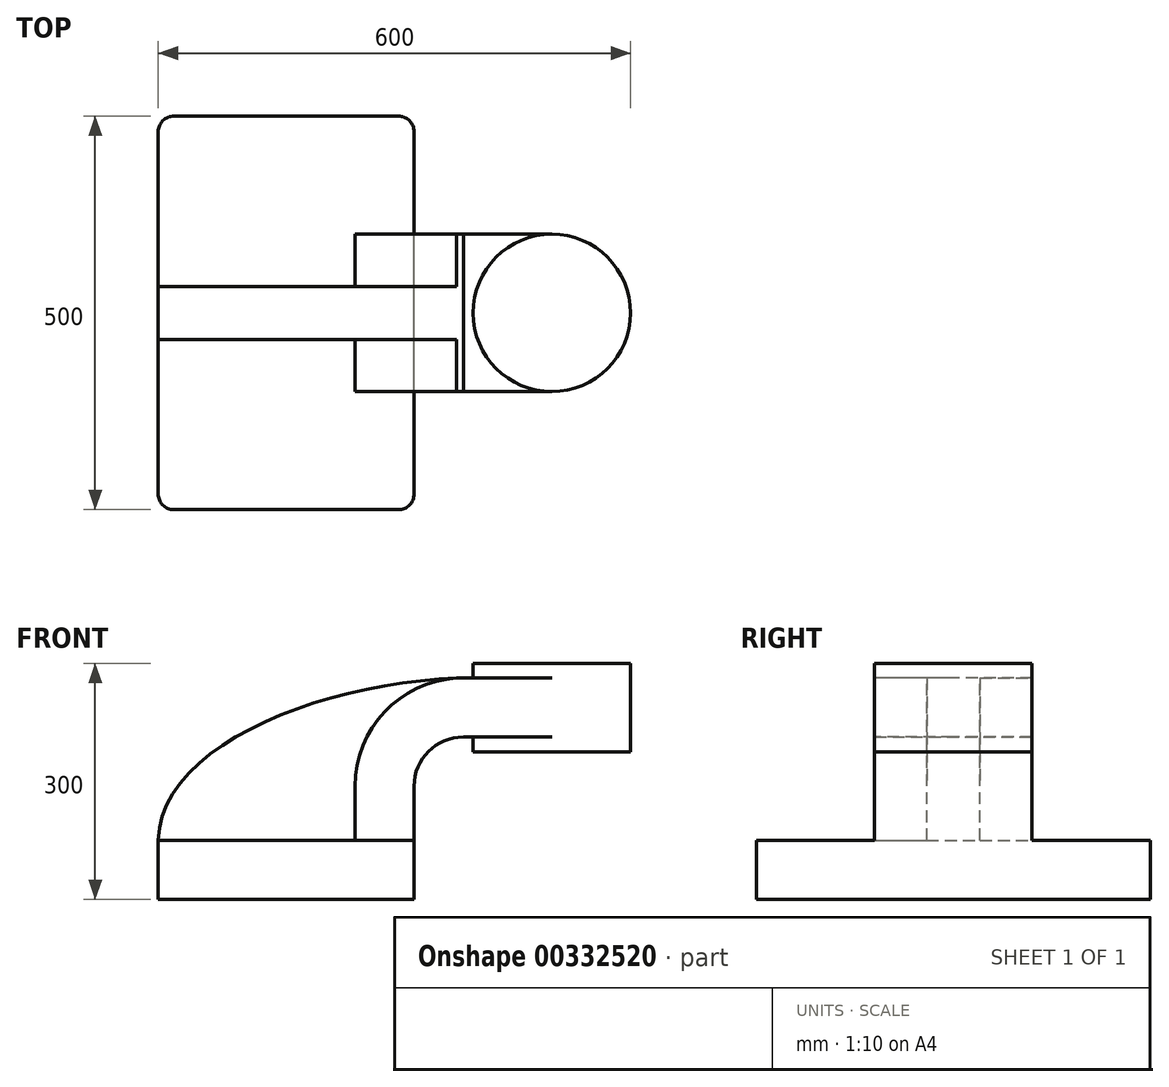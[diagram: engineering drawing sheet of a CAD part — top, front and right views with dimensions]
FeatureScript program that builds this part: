
annotation { "Feature Type Name" : "Feature", "Feature Type Description" : "" }
export const myFeature = defineFeature(function(context is Context, id is Id, definition is map)
    precondition{}
    {
        {
            var Q0;
            Q0=qCreatedBy(makeId("Front.planeOp"),FACE);
            var sketch = newSketch(context, id + "F0", { "sketchPlane" : qUnion([Q0])});
            skLineSegment(sketch, "E0.bottom", {"start": v(-162.5, -37.5) * mm, "end": v(162.5, -37.5) * mm});
            skLineSegment(sketch, "E0.top", {"start": v(-162.5, 37.5) * mm, "end": v(162.5, 37.5) * mm});
            skLineSegment(sketch, "E0.left", {"start": v(-162.5, -37.5) * mm, "end": v(-162.5, 37.5) * mm});
            skLineSegment(sketch, "E0.right", {"start": v(162.5, -37.5) * mm, "end": v(162.5, 37.5) * mm});
            skPoint(sketch, "E0.middle", {"position": v(0, 0) * mm});
            skLineSegment(sketch, "E1.bottom", {"start": v(437.5, 150) * mm, "end": v(237.5, 150) * mm});
            skLineSegment(sketch, "E1.top", {"start": v(437.5, 262.5) * mm, "end": v(237.5, 262.5) * mm});
            skLineSegment(sketch, "E1.left", {"start": v(437.5, 150) * mm, "end": v(437.5, 262.5) * mm});
            skLineSegment(sketch, "E1.right", {"start": v(237.5, 150) * mm, "end": v(237.5, 262.5) * mm});
            skPoint(sketch, "E1.middle", {"position": v(337.5, 206.25) * mm});
            skLineSegment(sketch, "E2", {"start": v(162.5, 37.5) * mm, "end": v(162.5, 106.3) * mm});
            skArc(sketch, "E3", {"start": v(162.5, 106.3) * mm, "mid": v(180.8, 150.5) * mm, "end": v(225, 168.8) * mm});
            skLineSegment(sketch, "E4", {"start": v(225, 168.8) * mm, "end": v(337.5, 168.8) * mm});
            skLineSegment(sketch, "E5.0", {"start": v(225, 243.8) * mm, "end": v(337.5, 243.8) * mm});
            skArc(sketch, "E5.1", {"start": v(87.5, 106.3) * mm, "mid": v(127.77, 203.53) * mm, "end": v(225, 243.8) * mm});
            skLineSegment(sketch, "E5.2", {"start": v(87.5, 37.5) * mm, "end": v(87.5, 106.3) * mm});
            skLineSegment(sketch, "E6", {"start": v(337.5, 150) * mm, "end": v(337.5, 262.5) * mm});
            skFitSpline(sketch, "E7", {"points": [v(-162.5, 37.5) * mm, v(225, 243.8) * mm], "startDerivative": vector(6.8, 368.5) * mm, "endDerivative": vector(520.4, 12.57) * mm});
            skSolve(sketch);
        }
        {
            var Q0;
            Q0=makeQuery(id+"F0.imprint","IMPRINT",FACE,{"disambiguationData":[TD([[makeQuery(id+"F0.imprint","IMPRINT",EDGE,{"derivedFrom":sQuery(id+"F0.wireOp",EDGE,"E0.bottom")}),1.0]])]});
            extrude(context, id + "F1", {"entities" : qUnion([Q0]), "endBound" : BoundingType.SYMMETRIC, "depth" : 500 * mm});
        }
        {
            var Q0;
            {var subQ1=sQuery(id+"F0.wireOp",EDGE,"E2");Q0=makeQuery(id+"F0.imprint","IMPRINT",FACE,{"disambiguationData":[TD([[makeQuery(id+"F0.imprint","IMPRINT",EDGE,{"derivedFrom":subQ1}),1.0]])]});}
            var Q1;
            {var subQ0=sQuery(id+"F0.wireOp",EDGE,"E4");var subQ1=sQuery(id+"F0.wireOp",EDGE,"E1.right");var subQ2=makeQuery(id+"F0.imprint","INTERSECT",VERTEX,{"derivedFrom":[subQ1,subQ0]});Q1=makeQuery(id+"F0.imprint","IMPRINT",FACE,{"disambiguationData":[TD([[makeQuery(id+"F0.imprint","IMPRINT",EDGE,{"disambiguationData":[TD([[subQ2,-1.0]])],"derivedFrom":subQ1}),-1.0]])]});}
            extrude(context, id + "F2", {"entities" : qUnion([Q0, Q1]), "operationType" : NewBodyOperationType.ADD, "endBound" : BoundingType.SYMMETRIC, "depth" : 200 * mm});
        }
        {
            var Q0;
            {var subQ3=sQuery(id+"F0.wireOp",EDGE,"E5.2");Q0=makeQuery(id+"F0.imprint","IMPRINT",FACE,{"disambiguationData":[TD([[makeQuery(id+"F0.imprint","IMPRINT",EDGE,{"derivedFrom":subQ3}),1.0]])]});}
            extrude(context, id + "F3", {"entities" : qUnion([Q0]), "operationType" : NewBodyOperationType.ADD, "endBound" : BoundingType.SYMMETRIC, "depth" : 67.5 * mm});
        }
        {
            var Q0;
            {var subQ0=sQuery(id+"F0.wireOp",EDGE,"E1.left");Q0=makeQuery(id+"F0.imprint","IMPRINT",FACE,{"disambiguationData":[TD([[makeQuery(id+"F0.imprint","IMPRINT",EDGE,{"derivedFrom":subQ0}),1.0]])]});}
            var Q1;
            Q1=sQuery(id+"F0.wireOp",EDGE,"E6");
            revolve(context, id + "F4", {"operationType" : NewBodyOperationType.ADD, "entities" : qUnion([Q0]), "axis" : qUnion([Q1]), "revolveType" : RevolveType.FULL});
        }
        {
            var Q0;
            Q0=makeQuery(id+"F1.opExtrude","CAP_EDGE",EDGE,{"disambiguationData":[OSD([sQuery(id+"F0.wireOp",EDGE,"E0.right")])],"isStart":false});
            var Q1;
            Q1=makeQuery(id+"F1.opExtrude","CAP_EDGE",EDGE,{"disambiguationData":[OSD([sQuery(id+"F0.wireOp",EDGE,"E0.left")])],"isStart":false});
            var Q2;
            Q2=makeQuery(id+"F1.opExtrude","CAP_EDGE",EDGE,{"disambiguationData":[OSD([sQuery(id+"F0.wireOp",EDGE,"E0.right")])],"isStart":true});
            var Q3;
            Q3=makeQuery(id+"F1.opExtrude","CAP_EDGE",EDGE,{"disambiguationData":[OSD([sQuery(id+"F0.wireOp",EDGE,"E0.left")])],"isStart":true});
            fillet(context, id + "F5", {"entities" : qUnion([Q0, Q1, Q2, Q3]), "radius" : 20 * mm, "tangentPropagation" : true, "allowEdgeOverflow" : false});
        }
    });
